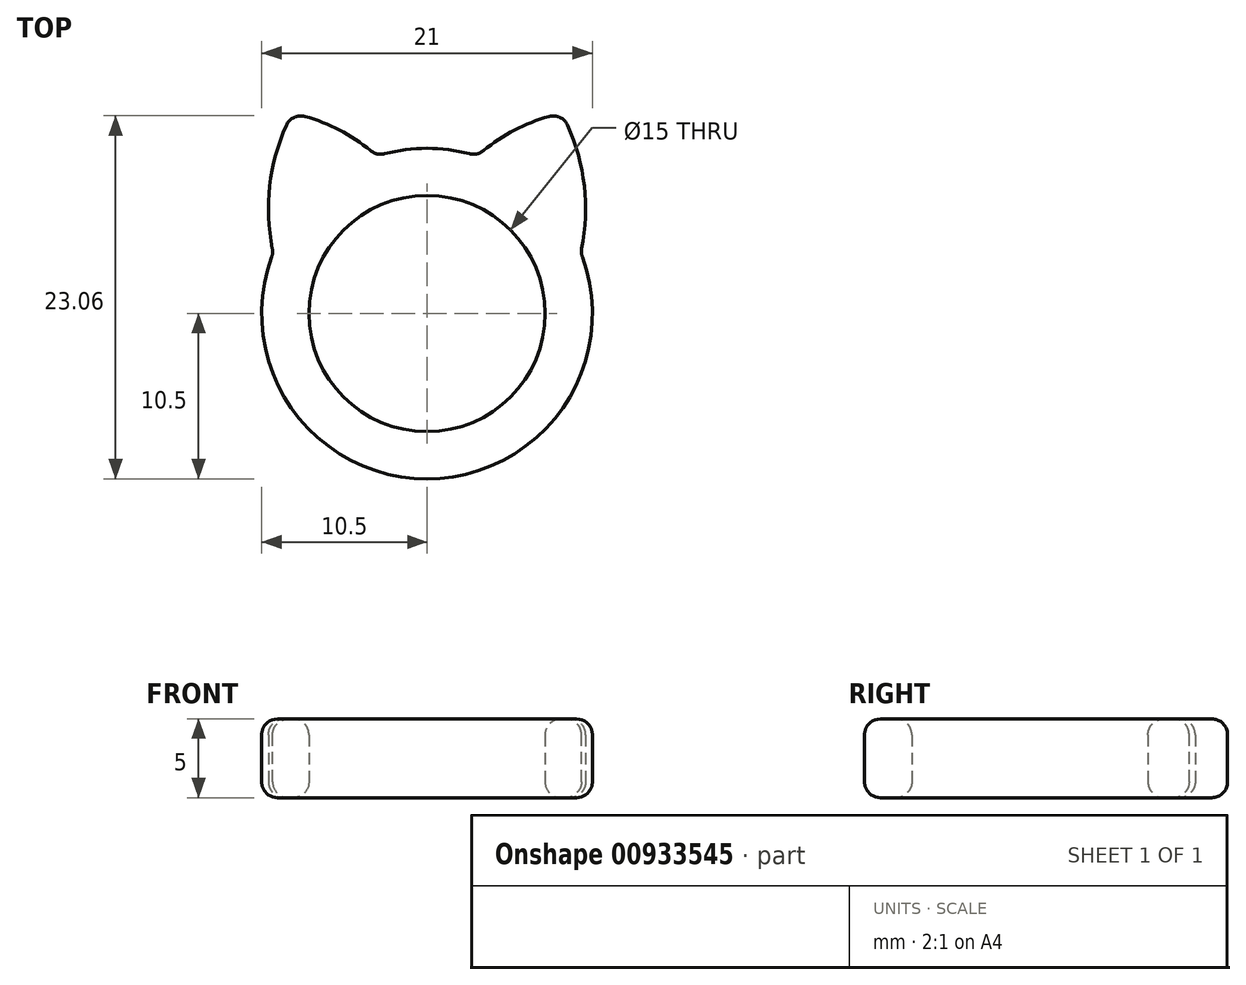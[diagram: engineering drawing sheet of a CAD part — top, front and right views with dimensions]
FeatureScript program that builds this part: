
annotation { "Feature Type Name" : "Feature", "Feature Type Description" : "" }
export const myFeature = defineFeature(function(context is Context, id is Id, definition is map)
    precondition{}
    {
        {
            var Q0;
            Q0=qCreatedBy(makeId("Top.planeOp"),FACE);
            var sketch = newSketch(context, id + "F0", { "sketchPlane" : qUnion([Q0])});
            skCircle(sketch, "E0", {"center": v(0, 0) * mm, "radius": 7.5 * mm});
            skCircle(sketch, "E1.0", {"center": v(0, 0) * mm, "radius": 10.5 * mm});
            skArc(sketch, "E2", {"start": v(-8.56, 12.72) * mm, "mid": v(-9.95, 8.39) * mm, "end": v(-9.77, 3.85) * mm});
            skArc(sketch, "E3.MirrorCS", {"start": v(8.56, 12.72) * mm, "mid": v(9.95, 8.39) * mm, "end": v(9.77, 3.85) * mm});
            skArc(sketch, "E4.trimOffspring", {"start": v(-3.2, 10) * mm, "mid": v(-5.7, 11.73) * mm, "end": v(-8.56, 12.72) * mm});
            skArc(sketch, "E5.trimOffspring", {"start": v(3.2, 10) * mm, "mid": v(5.7, 11.73) * mm, "end": v(8.56, 12.72) * mm});
            skLineSegment(sketch, "E6", {"start": v(0, 0) * mm, "end": v(0, 3.17) * mm, "construction": true});
            skLineSegment(sketch, "E7", {"start": v(9.77, 3.85) * mm, "end": v(-9.77, 3.85) * mm, "construction": true});
            skSolve(sketch);
        }
        {
            var Q0;
            Q0 = qSketchRegion(id + "F0", true);
            extrude(context, id + "F1", {"entities" : qUnion([Q0]), "depth" : 5 * mm, "offsetDistance" : 25 * mm});
        }
        {
            var Q0;
            Q0=makeQuery(id+"F1.opExtrude","CAP_FACE",FACE,{"disambiguationData":[OSD([sQuery(id+"F0.wireOp",EDGE,"E0"),sQuery(id+"F0.wireOp",EDGE,"E1.0"),sQuery(id+"F0.wireOp",EDGE,"E2"),sQuery(id+"F0.wireOp",EDGE,"E3.MirrorCS"),sQuery(id+"F0.wireOp",EDGE,"E4.trimOffspring"),sQuery(id+"F0.wireOp",EDGE,"E5.trimOffspring")])],"isStart":false});
            var Q1;
            Q1=makeQuery(id+"F1.opExtrude","CAP_FACE",FACE,{"disambiguationData":[OSD([sQuery(id+"F0.wireOp",EDGE,"E0"),sQuery(id+"F0.wireOp",EDGE,"E1.0"),sQuery(id+"F0.wireOp",EDGE,"E2"),sQuery(id+"F0.wireOp",EDGE,"E3.MirrorCS"),sQuery(id+"F0.wireOp",EDGE,"E4.trimOffspring"),sQuery(id+"F0.wireOp",EDGE,"E5.trimOffspring")])],"isStart":true});
            var Q2;
            Q2=makeQuery(id+"F1.opExtrude","SWEPT_EDGE",EDGE,{"disambiguationData":[OSD([sQuery(id+"F0.wireOp",EDGE,"E3.MirrorCS"),sQuery(id+"F0.wireOp",EDGE,"E5.trimOffspring")])]});
            var Q3;
            Q3=makeQuery(id+"F1.opExtrude","SWEPT_EDGE",EDGE,{"disambiguationData":[OSD([sQuery(id+"F0.wireOp",EDGE,"E2"),sQuery(id+"F0.wireOp",EDGE,"E4.trimOffspring")])]});
            var Q4;
            Q4=makeQuery(id+"F1.opExtrude","SWEPT_EDGE",EDGE,{"disambiguationData":[OSD([sQuery(id+"F0.wireOp",EDGE,"E1.0"),sQuery(id+"F0.wireOp",EDGE,"E3.MirrorCS")])]});
            var Q5;
            Q5=makeQuery(id+"F1.opExtrude","SWEPT_EDGE",EDGE,{"disambiguationData":[OSD([sQuery(id+"F0.wireOp",EDGE,"E1.0"),sQuery(id+"F0.wireOp",EDGE,"E2")])]});
            var Q6;
            Q6=makeQuery(id+"F1.opExtrude","SWEPT_EDGE",EDGE,{"disambiguationData":[OSD([sQuery(id+"F0.wireOp",EDGE,"E1.0"),sQuery(id+"F0.wireOp",EDGE,"E4.trimOffspring")])]});
            var Q7;
            Q7=makeQuery(id+"F1.opExtrude","SWEPT_EDGE",EDGE,{"disambiguationData":[OSD([sQuery(id+"F0.wireOp",EDGE,"E1.0"),sQuery(id+"F0.wireOp",EDGE,"E5.trimOffspring")])]});
            fillet(context, id + "F2", {"entities" : qUnion([Q0, Q1, Q2, Q3, Q4, Q5, Q6, Q7]), "tangentPropagation" : true, "radius" : 1 * mm, "defaultsChanged" : false, "vertexSettings" : [], "allowEdgeOverflow" : false});
        }
    });
